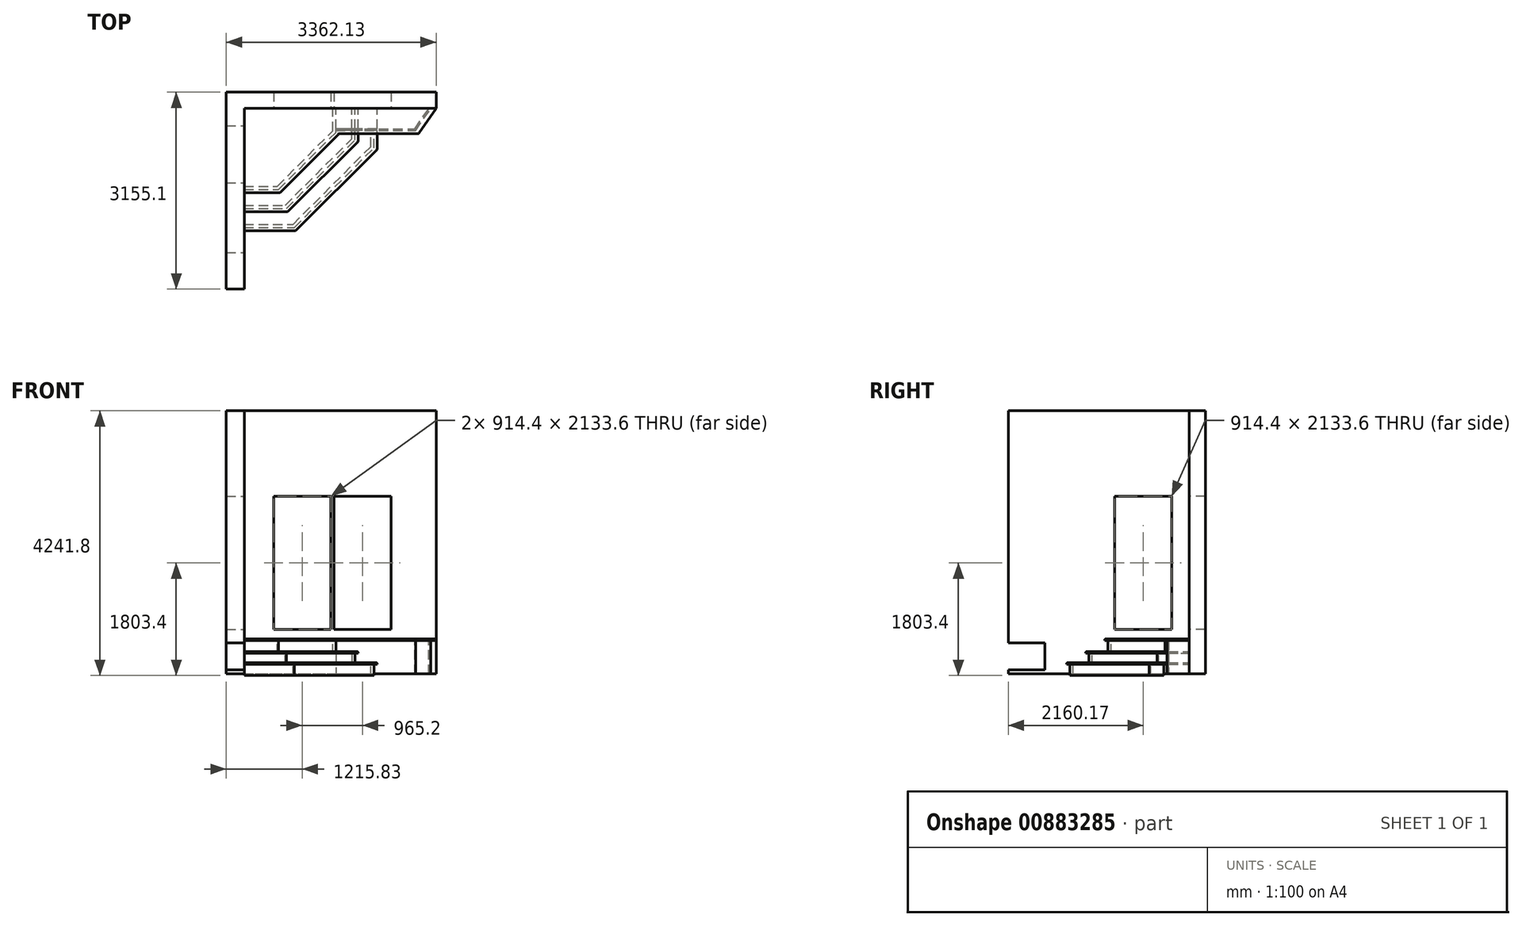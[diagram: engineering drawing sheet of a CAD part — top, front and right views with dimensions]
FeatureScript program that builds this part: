
annotation { "Feature Type Name" : "Feature", "Feature Type Description" : "" }
export const myFeature = defineFeature(function(context is Context, id is Id, definition is map)
    precondition{}
    {
        {
            var Q0;
            Q0=qCreatedBy(makeId("Top.planeOp"),FACE);
            var sketch = newSketch(context, id + "F0", { "sketchPlane" : qUnion([Q0])});
            skLineSegment(sketch, "E0.bottom", {"start": v(-1348, -2048.6) * mm, "end": v(-1636.72, -2048.6) * mm});
            skLineSegment(sketch, "E0.top", {"start": v(-1348, 1106.5) * mm, "end": v(-1636.72, 1106.5) * mm});
            skLineSegment(sketch, "E0.left", {"start": v(-1348, -2048.6) * mm, "end": v(-1348, 848.17) * mm});
            skLineSegment(sketch, "E0.right", {"start": v(-1636.72, -2048.6) * mm, "end": v(-1636.72, 1106.5) * mm});
            skLineSegment(sketch, "E1.bottom", {"start": v(-1348, 1106.5) * mm, "end": v(1725.4, 1106.5) * mm});
            skLineSegment(sketch, "E1.top", {"start": v(-1348, 848.17) * mm, "end": v(1725.4, 848.17) * mm});
            skLineSegment(sketch, "E1.right", {"start": v(1725.4, 1106.5) * mm, "end": v(1725.4, 848.17) * mm});
            skSolve(sketch);
        }
        {
            var Q0;
            Q0 = qSketchRegion(id + "F0", true);
            extrude(context, id + "F1", {"entities" : qUnion([Q0]), "depth" : 4216.4 * mm, "offsetDistance" : 25.4 * mm});
        }
        {
            var Q0;
            Q0=makeQuery(id+"F1.opExtrude","SWEPT_FACE",FACE,{"disambiguationData":[OSD([sQuery(id+"F0.wireOp",EDGE,"E0.left")])]});
            var sketch = newSketch(context, id + "F2", { "sketchPlane" : qUnion([Q0])});
            skLineSegment(sketch, "E2.bottom", {"start": v(-345.63, 711.2) * mm, "end": v(568.77, 711.2) * mm});
            skLineSegment(sketch, "E2.top", {"start": v(-345.63, 2844.8) * mm, "end": v(568.77, 2844.8) * mm});
            skLineSegment(sketch, "E2.left", {"start": v(-345.63, 711.2) * mm, "end": v(-345.63, 2844.8) * mm});
            skLineSegment(sketch, "E2.right", {"start": v(568.77, 711.2) * mm, "end": v(568.77, 2844.8) * mm});
            skSolve(sketch);
        }
        {
            var Q0;
            Q0 = qSketchRegion(id + "F2", true);
            extrude(context, id + "F3", {"entities" : qUnion([Q0]), "operationType" : NewBodyOperationType.REMOVE, "oppositeDirection" : true, "depth" : 3177.54 * mm, "offsetDistance" : 25.4 * mm});
        }
        {
            var Q0;
            Q0=makeQuery(id+"F1.opExtrude","SWEPT_FACE",FACE,{"disambiguationData":[OSD([sQuery(id+"F0.wireOp",EDGE,"E1.top")])]});
            var sketch = newSketch(context, id + "F4", { "sketchPlane" : qUnion([Q0])});
            skLineSegment(sketch, "E3.bottom", {"start": v(-878.1, 711.2) * mm, "end": v(36.3, 711.2) * mm});
            skLineSegment(sketch, "E3.top", {"start": v(-878.1, 2844.8) * mm, "end": v(36.3, 2844.8) * mm});
            skLineSegment(sketch, "E3.left", {"start": v(-878.1, 711.2) * mm, "end": v(-878.1, 2844.8) * mm});
            skLineSegment(sketch, "E3.right", {"start": v(36.3, 711.2) * mm, "end": v(36.3, 2844.8) * mm});
            skLineSegment(sketch, "E4.bottom", {"start": v(87.1, 711.2) * mm, "end": v(1001.5, 711.2) * mm});
            skLineSegment(sketch, "E4.top", {"start": v(87.1, 2844.8) * mm, "end": v(1001.5, 2844.8) * mm});
            skLineSegment(sketch, "E4.left", {"start": v(87.1, 711.2) * mm, "end": v(87.1, 2844.8) * mm});
            skLineSegment(sketch, "E4.right", {"start": v(1001.5, 711.2) * mm, "end": v(1001.5, 2844.8) * mm});
            skSolve(sketch);
        }
        {
            var Q0;
            Q0 = qSketchRegion(id + "F4", true);
            extrude(context, id + "F5", {"entities" : qUnion([Q0]), "operationType" : NewBodyOperationType.REMOVE, "endBound" : BoundingType.THROUGH_ALL, "oppositeDirection" : true, "depth" : 25.4 * mm, "offsetDistance" : 25.4 * mm});
        }
        {
            var Q0;
            Q0=qCreatedBy(makeId("Top.planeOp"),FACE);
            cPlane(context, id + "F6", {"entities" : qUnion([Q0]), "cplaneType" : CPlaneType.OFFSET, "offset" : 558.8 * mm, "width" : 152.4 * mm, "height" : 152.4 * mm});
        }
        {
            var Q0;
            Q0=qCreatedBy(id+"F6.planeOp",FACE);
            var sketch = newSketch(context, id + "F7", { "sketchPlane" : qUnion([Q0])});
            skPoint(sketch, "E5.0", {"position": v(-1348, 848.17) * mm});
            skLineSegment(sketch, "E5.1", {"start": v(-1348, -2048.6) * mm, "end": v(-1348, 848.17) * mm, "construction": true});
            skLineSegment(sketch, "E5.2", {"start": v(-1348, 848.17) * mm, "end": v(1725.4, 848.17) * mm, "construction": true});
            skLineSegment(sketch, "E6", {"start": v(-1348, 848.17) * mm, "end": v(-1348, -503.85) * mm});
            skLineSegment(sketch, "E7", {"start": v(-1348, -503.85) * mm, "end": v(-777.78, -503.85) * mm});
            skLineSegment(sketch, "E8", {"start": v(-777.78, -503.85) * mm, "end": v(167.83, 441.77) * mm});
            skLineSegment(sketch, "E9", {"start": v(167.83, 441.77) * mm, "end": v(167.83, 848.17) * mm});
            skLineSegment(sketch, "E10", {"start": v(167.83, 848.17) * mm, "end": v(-1348, 848.17) * mm});
            skPoint(sketch, "E11.0", {"position": v(-1348, -345.63) * mm});
            skPoint(sketch, "E12.0", {"position": v(36.3, 848.17) * mm});
            skSolve(sketch);
        }
        {
            var Q0;
            Q0=makeQuery(id+"F7.imprint","IMPRINT",FACE,{"disambiguationData":[TD([[makeQuery(id+"F7.imprint","IMPRINT",EDGE,{"derivedFrom":sQuery(id+"F7.wireOp",EDGE,"E6")}),1.0]])]});
            extrude(context, id + "F8", {"entities" : qUnion([Q0]), "oppositeDirection" : true, "depth" : 25.4 * mm, "offsetDistance" : 25.4 * mm});
        }
        {
            var Q0;
            Q0=makeQuery(id+"F8.opExtrude","CAP_FACE",FACE,{"disambiguationData":[OSD([sQuery(id+"F7.wireOp",EDGE,"E6"),sQuery(id+"F7.wireOp",EDGE,"E7"),sQuery(id+"F7.wireOp",EDGE,"E8"),sQuery(id+"F7.wireOp",EDGE,"E9"),sQuery(id+"F7.wireOp",EDGE,"E10")])],"isStart":false});
            var sketch = newSketch(context, id + "F9", { "sketchPlane" : qUnion([Q0])});
            skLineSegment(sketch, "E13.0", {"start": v(117.03, -462.8) * mm, "end": v(117.03, -848.17) * mm});
            skLineSegment(sketch, "E13.1", {"start": v(-798.82, 453.05) * mm, "end": v(117.03, -462.8) * mm});
            skLineSegment(sketch, "E13.2", {"start": v(-1348, 453.05) * mm, "end": v(-798.82, 453.05) * mm});
            skLineSegment(sketch, "E14.0", {"start": v(66.23, -483.85) * mm, "end": v(66.23, -848.17) * mm});
            skLineSegment(sketch, "E14.1", {"start": v(-819.87, 402.25) * mm, "end": v(66.23, -483.85) * mm});
            skLineSegment(sketch, "E14.2", {"start": v(-1348, 402.25) * mm, "end": v(-819.87, 402.25) * mm});
            skLineSegment(sketch, "E15", {"start": v(-1348, 402.25) * mm, "end": v(-1348, 453.05) * mm});
            skLineSegment(sketch, "E16", {"start": v(66.23, -848.17) * mm, "end": v(117.03, -848.17) * mm});
            skSolve(sketch);
        }
        {
            var Q0;
            Q0 = qSketchRegion(id + "F9", true);
            extrude(context, id + "F10", {"entities" : qUnion([Q0]), "operationType" : NewBodyOperationType.ADD, "depth" : 177.8 * mm, "offsetDistance" : 25.4 * mm});
        }
        {
            var Q0;
            Q0=makeQuery(id+"F10.opExtrude","CAP_FACE",FACE,{"disambiguationData":[OSD([sQuery(id+"F9.wireOp",EDGE,"E13.0"),sQuery(id+"F9.wireOp",EDGE,"E13.1"),sQuery(id+"F9.wireOp",EDGE,"E13.2"),sQuery(id+"F9.wireOp",EDGE,"E14.0"),sQuery(id+"F9.wireOp",EDGE,"E14.1"),sQuery(id+"F9.wireOp",EDGE,"E14.2"),sQuery(id+"F9.wireOp",EDGE,"E15"),sQuery(id+"F9.wireOp",EDGE,"E16")])],"isStart":false});
            var sketch = newSketch(context, id + "F11", { "sketchPlane" : qUnion([Q0])});
            skLineSegment(sketch, "E17.0", {"start": v(472.63, -315.52) * mm, "end": v(472.63, -848.17) * mm});
            skLineSegment(sketch, "E17.1", {"start": v(-651.53, 808.65) * mm, "end": v(472.63, -315.52) * mm});
            skLineSegment(sketch, "E17.2", {"start": v(-1348, 808.65) * mm, "end": v(-651.53, 808.65) * mm});
            skLineSegment(sketch, "E18.0", {"start": v(-1348, 402.25) * mm, "end": v(-819.87, 402.25) * mm});
            skLineSegment(sketch, "E18.1", {"start": v(-819.87, 402.25) * mm, "end": v(66.23, -483.85) * mm});
            skLineSegment(sketch, "E18.2", {"start": v(66.23, -483.85) * mm, "end": v(66.23, -848.17) * mm});
            skLineSegment(sketch, "E19", {"start": v(66.23, -848.17) * mm, "end": v(472.63, -848.17) * mm});
            skLineSegment(sketch, "E20", {"start": v(-1348, 402.25) * mm, "end": v(-1348, 808.65) * mm});
            skSolve(sketch);
        }
        {
            var Q0;
            {var subQ2=sQuery(id+"F11.wireOp",EDGE,"E17.0");Q0=makeQuery(id+"F11.imprint","IMPRINT",FACE,{"disambiguationData":[TD([[makeQuery(id+"F11.imprint","IMPRINT",EDGE,{"derivedFrom":subQ2}),-1.0]])]});}
            var Q1;
            Q1 = qSketchRegion(id + "F11", true);
            extrude(context, id + "F12", {"entities" : qUnion([Q0, Q1]), "operationType" : NewBodyOperationType.ADD, "depth" : 25.4 * mm, "offsetDistance" : 25.4 * mm});
        }
        {
            var Q0;
            Q0=makeQuery(id+"F12.opExtrude","CAP_FACE",FACE,{"disambiguationData":[OSD([sQuery(id+"F11.wireOp",EDGE,"E17.0"),sQuery(id+"F11.wireOp",EDGE,"E17.1"),sQuery(id+"F11.wireOp",EDGE,"E17.2"),sQuery(id+"F11.wireOp",EDGE,"E18.0"),sQuery(id+"F11.wireOp",EDGE,"E18.1"),sQuery(id+"F11.wireOp",EDGE,"E18.2"),sQuery(id+"F11.wireOp",EDGE,"E19"),sQuery(id+"F11.wireOp",EDGE,"E20")])],"isStart":false});
            var sketch = newSketch(context, id + "F13", { "sketchPlane" : qUnion([Q0])});
            skLineSegment(sketch, "E21.0", {"start": v(421.83, -336.56) * mm, "end": v(421.83, -848.17) * mm});
            skLineSegment(sketch, "E21.1", {"start": v(-672.57, 757.85) * mm, "end": v(421.83, -336.56) * mm});
            skLineSegment(sketch, "E21.2", {"start": v(-1348, 757.85) * mm, "end": v(-672.57, 757.85) * mm});
            skLineSegment(sketch, "E22.0", {"start": v(371.03, -357.6) * mm, "end": v(371.03, -848.17) * mm});
            skLineSegment(sketch, "E22.1", {"start": v(-693.61, 707.05) * mm, "end": v(371.03, -357.6) * mm});
            skLineSegment(sketch, "E22.2", {"start": v(-1348, 707.05) * mm, "end": v(-693.61, 707.05) * mm});
            skLineSegment(sketch, "E23", {"start": v(-1348, 757.85) * mm, "end": v(-1348, 707.05) * mm});
            skLineSegment(sketch, "E24", {"start": v(371.03, -848.17) * mm, "end": v(421.83, -848.17) * mm});
            skSolve(sketch);
        }
        {
            var Q0;
            Q0 = qSketchRegion(id + "F13", true);
            extrude(context, id + "F14", {"entities" : qUnion([Q0]), "operationType" : NewBodyOperationType.ADD, "depth" : 152.4 * mm, "offsetDistance" : 25.4 * mm});
        }
        {
            var Q0;
            Q0=makeQuery(id+"F14.opExtrude","CAP_FACE",FACE,{"disambiguationData":[OSD([sQuery(id+"F13.wireOp",EDGE,"E21.0"),sQuery(id+"F13.wireOp",EDGE,"E21.1"),sQuery(id+"F13.wireOp",EDGE,"E21.2"),sQuery(id+"F13.wireOp",EDGE,"E22.0"),sQuery(id+"F13.wireOp",EDGE,"E22.1"),sQuery(id+"F13.wireOp",EDGE,"E22.2"),sQuery(id+"F13.wireOp",EDGE,"E23"),sQuery(id+"F13.wireOp",EDGE,"E24")])],"isStart":false});
            var sketch = newSketch(context, id + "F15", { "sketchPlane" : qUnion([Q0])});
            skLineSegment(sketch, "E25.0", {"start": v(777.43, -189.26) * mm, "end": v(777.43, -848.17) * mm});
            skLineSegment(sketch, "E25.1", {"start": v(-525.28, 1113.45) * mm, "end": v(777.43, -189.26) * mm});
            skLineSegment(sketch, "E25.2", {"start": v(-1348, 1113.45) * mm, "end": v(-525.28, 1113.45) * mm});
            skLineSegment(sketch, "E26.0", {"start": v(-1348, 707.05) * mm, "end": v(-693.61, 707.05) * mm});
            skLineSegment(sketch, "E26.1", {"start": v(-693.61, 707.05) * mm, "end": v(371.03, -357.6) * mm});
            skLineSegment(sketch, "E26.2", {"start": v(371.03, -357.6) * mm, "end": v(371.03, -848.17) * mm});
            skLineSegment(sketch, "E27", {"start": v(371.03, -848.17) * mm, "end": v(777.43, -848.17) * mm});
            skLineSegment(sketch, "E28", {"start": v(-1348, 707.05) * mm, "end": v(-1348, 1113.45) * mm});
            skSolve(sketch);
        }
        {
            var Q0;
            Q0 = qSketchRegion(id + "F15", true);
            extrude(context, id + "F16", {"entities" : qUnion([Q0]), "operationType" : NewBodyOperationType.ADD, "depth" : 25.4 * mm, "offsetDistance" : 25.4 * mm});
        }
        {
            var Q0;
            Q0=makeQuery(id+"F8.opExtrude","CAP_FACE",FACE,{"disambiguationData":[OSD([sQuery(id+"F7.wireOp",EDGE,"E6"),sQuery(id+"F7.wireOp",EDGE,"E7"),sQuery(id+"F7.wireOp",EDGE,"E8"),sQuery(id+"F7.wireOp",EDGE,"E9"),sQuery(id+"F7.wireOp",EDGE,"E10")])],"isStart":true});
            var sketch = newSketch(context, id + "F17", { "sketchPlane" : qUnion([Q0])});
            skLineSegment(sketch, "E29.bottom", {"start": v(167.83, 441.77) * mm, "end": v(1446, 441.77) * mm});
            skLineSegment(sketch, "E29.top", {"start": v(167.83, 848.17) * mm, "end": v(1725.4, 848.17) * mm});
            skLineSegment(sketch, "E29.left", {"start": v(167.83, 441.77) * mm, "end": v(167.83, 848.17) * mm});
            skLineSegment(sketch, "E30", {"start": v(1446, 441.77) * mm, "end": v(1725.4, 848.17) * mm});
            skPoint(sketch, "E31.0", {"position": v(1725.4, 848.17) * mm});
            skPoint(sketch, "E29.right.start.orphan", {"position": v(1725.4, 441.77) * mm});
            skSolve(sketch);
        }
        {
            var Q0;
            Q0=makeQuery(id+"F17.imprint","IMPRINT",FACE,{"disambiguationData":[TD([[makeQuery(id+"F17.imprint","IMPRINT",EDGE,{"derivedFrom":sQuery(id+"F17.wireOp",EDGE,"E29.bottom")}),1.0]])]});
            extrude(context, id + "F18", {"entities" : qUnion([Q0]), "operationType" : NewBodyOperationType.ADD, "oppositeDirection" : true, "depth" : 25.4 * mm, "offsetDistance" : 25.4 * mm});
        }
        {
            var Q0;
            {var subQ0=sQuery(id+"F15.wireOp",EDGE,"E25.1");var subQ1=sQuery(id+"F15.wireOp",EDGE,"E25.2");var subQ2=sQuery(id+"F15.wireOp",EDGE,"E26.1");var subQ3=sQuery(id+"F15.wireOp",EDGE,"E25.0");var subQ4=sQuery(id+"F15.wireOp",EDGE,"E26.0");var subQ5=sQuery(id+"F15.wireOp",EDGE,"E26.2");var subQ6=sQuery(id+"F15.wireOp",EDGE,"E28");Q0=makeQuery(id+"FbDBVisBIPUHrdv_2.boolean.opBoolean","SPLIT",FACE,{"disambiguationData":[TD([makeQuery(id+"F8.opExtrude","SWEPT_FACE",FACE,{"disambiguationData":[OSD([sQuery(id+"F7.wireOp",EDGE,"E6")])]})])],"derivedFrom":makeQuery(id+"F16.opExtrude","CAP_FACE",FACE,{"disambiguationData":[OSD([subQ3,subQ0,subQ1,subQ4,subQ2,subQ5,sQuery(id+"F15.wireOp",EDGE,"E27"),subQ6])],"isStart":false})});}
            var sketch = newSketch(context, id + "F19", { "sketchPlane" : qUnion([Q0])});
            skLineSegment(sketch, "E32.0", {"start": v(726.63, -210.3) * mm, "end": v(726.63, -441.77) * mm});
            skLineSegment(sketch, "E32.1", {"start": v(-546.32, 1062.65) * mm, "end": v(726.63, -210.3) * mm});
            skLineSegment(sketch, "E32.2", {"start": v(-1348, 1062.65) * mm, "end": v(-546.32, 1062.65) * mm});
            skLineSegment(sketch, "E33.0", {"start": v(675.83, -231.35) * mm, "end": v(675.83, -441.77) * mm});
            skLineSegment(sketch, "E33.1", {"start": v(-567.36, 1011.85) * mm, "end": v(675.83, -231.35) * mm});
            skLineSegment(sketch, "E33.2", {"start": v(-1348, 1011.85) * mm, "end": v(-567.36, 1011.85) * mm});
            skLineSegment(sketch, "E34", {"start": v(-1348, 1062.65) * mm, "end": v(-1348, 1011.85) * mm});
            skLineSegment(sketch, "E35", {"start": v(675.83, -441.77) * mm, "end": v(726.63, -441.77) * mm});
            skSolve(sketch);
        }
        {
            var Q0;
            Q0 = qSketchRegion(id + "F19", true);
            extrude(context, id + "F20", {"entities" : qUnion([Q0]), "operationType" : NewBodyOperationType.ADD, "depth" : 177.8 * mm, "offsetDistance" : 25.4 * mm});
        }
        {
            var Q0;
            Q0=makeQuery(id+"F18.opExtrude","SWEPT_FACE",FACE,{"disambiguationData":[OSD([sQuery(id+"F17.wireOp",EDGE,"E29.bottom")])]});
            cPlane(context, id + "F21", {"entities" : qUnion([Q0]), "cplaneType" : CPlaneType.OFFSET, "offset" : 50.8 * mm, "oppositeDirection" : true, "width" : 152.4 * mm, "height" : 152.4 * mm});
        }
        {
            var Q0;
            Q0=qCreatedBy(id+"F21.planeOp",FACE);
            var sketch = newSketch(context, id + "F22", { "sketchPlane" : qUnion([Q0])});
            skPoint(sketch, "E36.0", {"position": v(117.03, 533.4) * mm});
            skLineSegment(sketch, "E37.bottom", {"start": v(117.03, 533.4) * mm, "end": v(1395.2, 533.4) * mm});
            skLineSegment(sketch, "E37.top", {"start": v(117.03, 0) * mm, "end": v(1395.2, 0) * mm});
            skLineSegment(sketch, "E37.left", {"start": v(117.03, 533.4) * mm, "end": v(117.03, 0) * mm});
            skLineSegment(sketch, "E37.right", {"start": v(1395.2, 533.4) * mm, "end": v(1395.2, 0) * mm});
            skSolve(sketch);
        }
        {
            var Q0;
            Q0=makeQuery(id+"F22.imprint","IMPRINT",FACE,{"disambiguationData":[TD([[makeQuery(id+"F22.imprint","IMPRINT",EDGE,{"derivedFrom":sQuery(id+"F22.wireOp",EDGE,"E37.bottom")}),-1.0]])]});
            var Q1;
            Q1 = qSketchRegion(id + "F22", true);
            extrude(context, id + "F23", {"entities" : qUnion([Q0, Q1]), "operationType" : NewBodyOperationType.ADD, "oppositeDirection" : true, "depth" : 25.4 * mm, "offsetDistance" : 25.4 * mm});
        }
        {
            var Q0;
            Q0=makeQuery(id+"F8.opExtrude","CAP_EDGE",EDGE,{"disambiguationData":[OSD([sQuery(id+"F7.wireOp",EDGE,"E7")])],"isStart":true});
            var Q1;
            Q1=makeQuery(id+"F8.opExtrude","CAP_EDGE",EDGE,{"disambiguationData":[OSD([sQuery(id+"F7.wireOp",EDGE,"E8")])],"isStart":true});
            var Q2;
            Q2=makeQuery(id+"F12.opExtrude","CAP_EDGE",EDGE,{"disambiguationData":[OSD([sQuery(id+"F11.wireOp",EDGE,"E17.2")])],"isStart":true});
            var Q3;
            Q3=makeQuery(id+"F12.opExtrude","CAP_EDGE",EDGE,{"disambiguationData":[OSD([sQuery(id+"F11.wireOp",EDGE,"E17.1")])],"isStart":true});
            var Q4;
            Q4=makeQuery(id+"F16.opExtrude","CAP_EDGE",EDGE,{"disambiguationData":[OSD([sQuery(id+"F15.wireOp",EDGE,"E25.2")])],"isStart":true});
            var Q5;
            Q5=makeQuery(id+"F16.opExtrude","CAP_EDGE",EDGE,{"disambiguationData":[OSD([sQuery(id+"F15.wireOp",EDGE,"E25.1")])],"isStart":true});
            var Q6;
            Q6=makeQuery(id+"F18.opExtrude","CAP_EDGE",EDGE,{"disambiguationData":[OSD([sQuery(id+"F17.wireOp",EDGE,"E29.bottom")])],"isStart":true});
            var Q7;
            {var subQ0=sQuery(id+"F11.wireOp",EDGE,"E17.0");var subQ1=sQuery(id+"F11.wireOp",EDGE,"E17.1");Q7=makeQuery(id+"F23.boolean.opBoolean","SPLIT",EDGE,{"disambiguationData":[TD([makeQuery(id+"F12.opExtrude","SWEPT_FACE",FACE,{"disambiguationData":[OSD([subQ1])]})])],"derivedFrom":makeQuery(id+"F12.opExtrude","CAP_EDGE",EDGE,{"disambiguationData":[OSD([subQ0])],"isStart":true})});}
            var Q8;
            {var subQ0=sQuery(id+"F15.wireOp",EDGE,"E25.0");var subQ1=sQuery(id+"F15.wireOp",EDGE,"E25.1");Q8=makeQuery(id+"F23.boolean.opBoolean","SPLIT",EDGE,{"disambiguationData":[TD([makeQuery(id+"F16.opExtrude","SWEPT_FACE",FACE,{"disambiguationData":[OSD([subQ1])]})])],"derivedFrom":makeQuery(id+"F16.opExtrude","CAP_EDGE",EDGE,{"disambiguationData":[OSD([subQ0])],"isStart":true})});}
            var Q9;
            Q9=makeQuery(id+"F18.opExtrude","CAP_EDGE",EDGE,{"disambiguationData":[OSD([sQuery(id+"F17.wireOp",EDGE,"E30")])],"isStart":true});
            fillet(context, id + "F24", {"entities" : qUnion([Q0, Q1, Q2, Q3, Q4, Q5, Q6, Q7, Q8, Q9]), "radius" : 12.7 * mm, "tangentPropagation" : true, "allowEdgeOverflow" : false});
        }
        {
            var Q0;
            {var subQ0=sQuery(id+"F7.wireOp",EDGE,"E8");var subQ1=sQuery(id+"F7.wireOp",EDGE,"E7");var subQ2=sQuery(id+"F7.wireOp",EDGE,"E9");var subQ3=sQuery(id+"F7.wireOp",EDGE,"E6");var subQ4=sQuery(id+"F7.wireOp",EDGE,"E10");Q0=makeQuery(id+"F18.boolean.opBoolean","MERGE",FACE,{"derivedFrom":[makeQuery(id+"F10.boolean.opBoolean","SPLIT",FACE,{"disambiguationData":[TD([makeQuery(id+"F8.opExtrude","SWEPT_FACE",FACE,{"disambiguationData":[OSD([subQ1])]})])],"derivedFrom":makeQuery(id+"F8.opExtrude","CAP_FACE",FACE,{"disambiguationData":[OSD([subQ3,subQ1,subQ0,subQ2,subQ4])],"isStart":false})}),makeQuery(id+"F18.opExtrude","CAP_FACE",FACE,{"disambiguationData":[OSD([sQuery(id+"F17.wireOp",EDGE,"E29.bottom"),sQuery(id+"F17.wireOp",EDGE,"E29.top"),sQuery(id+"F17.wireOp",EDGE,"E29.left"),sQuery(id+"F17.wireOp",EDGE,"E30")])],"isStart":false})]});}
            var sketch = newSketch(context, id + "F25", { "sketchPlane" : qUnion([Q0])});
            skLineSegment(sketch, "E38.0", {"start": v(1395.2, -492.57) * mm, "end": v(1639.68, -848.17) * mm});
            skLineSegment(sketch, "E39.0", {"start": v(1374.28, -506.96) * mm, "end": v(1608.86, -848.17) * mm});
            skLineSegment(sketch, "E40", {"start": v(1374.28, -506.96) * mm, "end": v(1395.2, -492.57) * mm});
            skLineSegment(sketch, "E41", {"start": v(1639.68, -848.17) * mm, "end": v(1608.86, -848.17) * mm});
            skSolve(sketch);
        }
        {
            var Q0;
            Q0 = qSketchRegion(id + "F25", true);
            var Q1;
            Q1=makeQuery(id+"F23.opExtrude","SWEPT_FACE",FACE,{"disambiguationData":[OSD([sQuery(id+"F22.wireOp",EDGE,"E37.top")])]});
            extrude(context, id + "F26", {"entities" : qUnion([Q0]), "operationType" : NewBodyOperationType.ADD, "endBound" : BoundingType.UP_TO_SURFACE, "depth" : 566.42 * mm, "endBoundEntityFace" : qUnion([Q1]), "offsetDistance" : 25.4 * mm});
        }
        {
            var Q0;
            Q0=makeQuery(id+"F1.opExtrude","SWEPT_FACE",FACE,{"disambiguationData":[OSD([sQuery(id+"F0.wireOp",EDGE,"E0.left")])]});
            var sketch = newSketch(context, id + "F27", { "sketchPlane" : qUnion([Q0])});
            skLineSegment(sketch, "E42.bottom", {"start": v(-1463.23, 61.88) * mm, "end": v(-2377.63, 61.88) * mm});
            skLineSegment(sketch, "E42.top", {"start": v(-1463.23, 498.86) * mm, "end": v(-2377.63, 498.86) * mm});
            skLineSegment(sketch, "E42.left", {"start": v(-1463.23, 61.88) * mm, "end": v(-1463.23, 498.86) * mm});
            skLineSegment(sketch, "E42.right", {"start": v(-2377.63, 61.88) * mm, "end": v(-2377.63, 498.86) * mm});
            skSolve(sketch);
        }
        {
            var Q0;
            Q0 = qSketchRegion(id + "F27", true);
            extrude(context, id + "F28", {"entities" : qUnion([Q0]), "operationType" : NewBodyOperationType.REMOVE, "endBound" : BoundingType.THROUGH_ALL, "oppositeDirection" : true, "depth" : 25.4 * mm, "offsetDistance" : 25.4 * mm});
        }
        {
            var Q0;
            Q0=makeQuery(id+"F24.opFillet","BLEND_EDGE",EDGE,{"blendedFrom":[makeQuery(id+"F18.opExtrude","CAP_EDGE",EDGE,{"disambiguationData":[OSD([sQuery(id+"F17.wireOp",EDGE,"E29.bottom")])],"isStart":true}),makeQuery(id+"F18.opExtrude","CAP_EDGE",EDGE,{"disambiguationData":[OSD([sQuery(id+"F17.wireOp",EDGE,"E30")])],"isStart":true})],"blendedInto":[]});
            fillet(context, id + "F29", {"entities" : qUnion([Q0]), "radius" : 12.7 * mm, "tangentPropagation" : true, "allowEdgeOverflow" : false});
        }
    });
